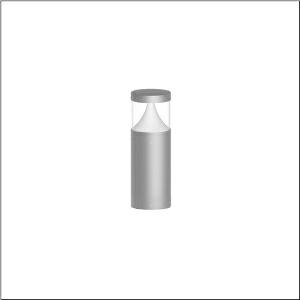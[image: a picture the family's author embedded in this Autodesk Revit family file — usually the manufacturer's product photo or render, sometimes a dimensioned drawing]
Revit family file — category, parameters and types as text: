
# Revit family: cl_31_poller_40_5cl424603
name_source: partatom
category: Lighting Fixtures
units: mm (PartAtom-declared; Revit-internal decimal feet)

## family parameters
Cut with Voids When Loaded = No
Host = Face
Light Source = No
Part Type = Normal
Room Calculation Point = No
Round Connector Dimension = Use Diameter
Shared = No

## types (1)
- --- (1 x LED, 800 lm, 7.2 W, 3000K)
    Apparent Load = 7 VA
    CIE Flux Codes = 19 66 88 92 100
    Color Rendering = 80
    Color Temperature = 3000K
    Default Elevation = 1800 mm
    Description = CL 31 Bollard 40, bollard luminaire, primary light control with lens, of PC, primary optical cover: cover panel, of PC, transparent, secondary light control with reflector, of PC, primary light characteristic: asymmetric, LED, rated luminous flux: 800lm, luminous efficacy: 110lm/W, light colour: 830, colour temperature: 3000K, control gear: ECG DALI, with terminal, 5-pole, max. 2.5mm², mains connection: 220..240V, AC, 50/60Hz, rated input power: 7.2W, luminaire housing, of aluminium, powder-coated, Siteco® metallic grey, diameter: 170mm, height: 400mm, protection rating (complete): IP65, insulation class (complete): insulation class I (protective earthing), certification: CE, ENEC, impact resistance: IK10, permissible operating ambient temperature for outdoor applications: -20..+50°C, packaging unit: 1 piece
    Height = 200 mm  [stored 0.656168 ft]
    Lamp = 1 x LED
    Lamp Light Flux = 800 lm
    Lamp Power = 7.2 W
    Lamp count = 1
    Length = 170 mm  [stored 0.557743 ft]
    Luminous efficacy = 111 lm/W
    Manufacturer = Siteco
    ModVariant = No
    Model = 5CL424603
    Mounting Place = Floor
    Mounting Type = Freestanding
    Number of Poles = 1
    OnlyDefault = Yes
    Power Factor = 1
    Product Name = CL 31 Poller 40
    Product group = bollard luminaire
    ProductGroupID = 1304
    Protection Class = Protection class I
    Protection Degree = IP 65
    RLX_Detail_Level = 1
    RLX_Emergency_Light_Flux = 0 lm
    RLX_Emergency_Type = 0
    RLX_Emergency_Type_DB = No
    RlxData = <blob elided: 62233 chars, md5=99988b8b>
    Socket = socket
    Standby Power = 0 W
    System Light Flux = 800 lm
    System Power = 7 W
    Type Comments = factory setting: luminous flux: 100 % | dim-lin: 254 | 182 mA
    Type Image = l_1006907.jpg
    URL = http://relux.com
    VarID = @adj_148411
    Voltage = 0 V
    Weight = 0.00 kg
    Width = 0 mm  [stored 0 ft]

note: [stored X ft] marks values corroborated as IEEE doubles in the binary element streams (Revit-internal decimal feet)

## geometry (parser evidence)
native form markers: Blend x4, Sweep x12
no freeform markers — native parametric forms only
